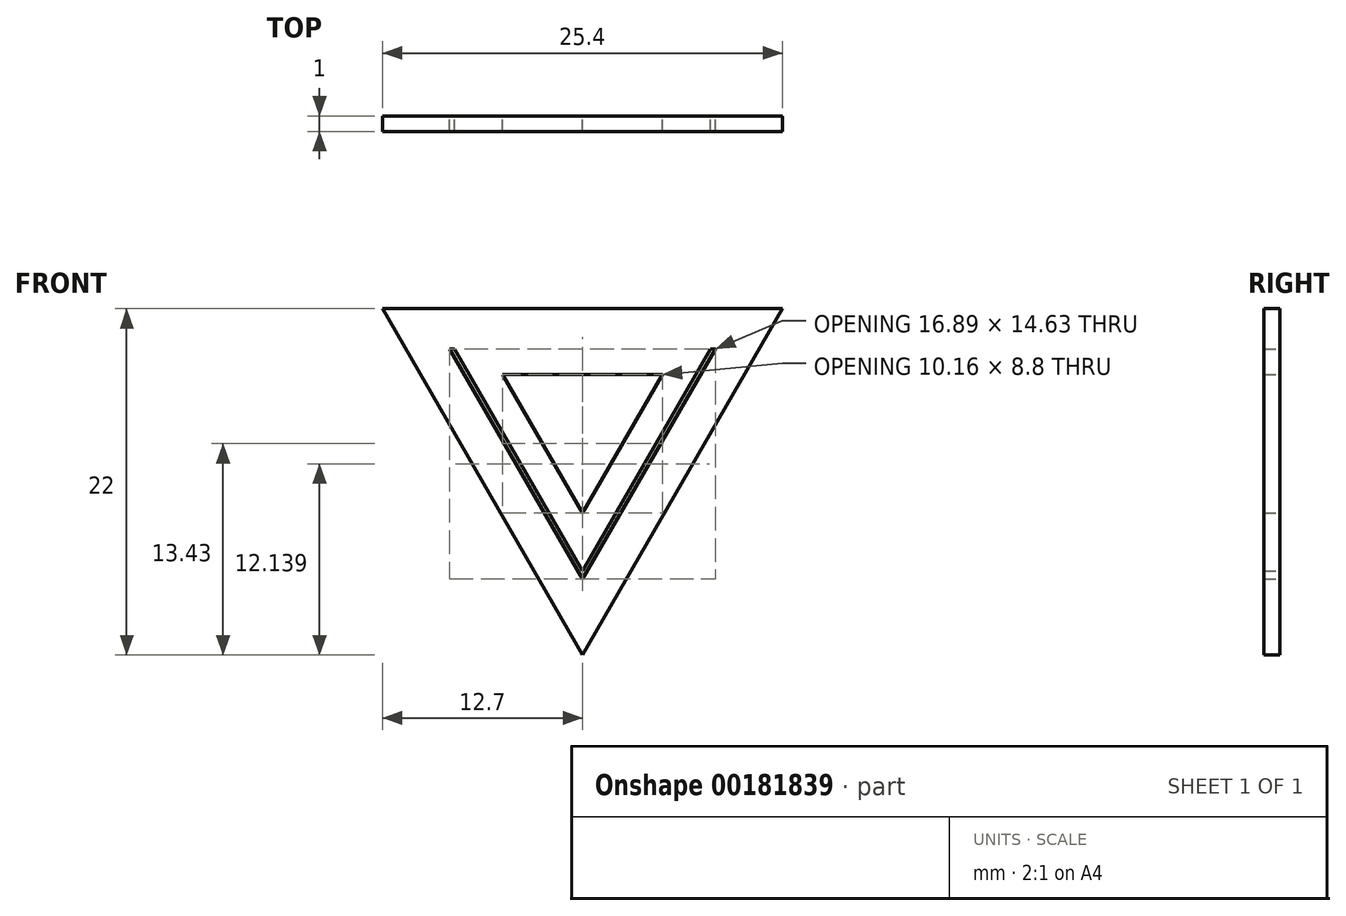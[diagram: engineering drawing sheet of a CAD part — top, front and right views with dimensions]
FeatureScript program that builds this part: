
annotation { "Feature Type Name" : "Feature", "Feature Type Description" : "" }
export const myFeature = defineFeature(function(context is Context, id is Id, definition is map)
    precondition{}
    {
        {
            var Q0;
            Q0=qCreatedBy(makeId("Front.planeOp"),FACE);
            var sketch = newSketch(context, id + "F0", { "sketchPlane" : qUnion([Q0])});
            skLineSegment(sketch, "E0", {"start": v(-12.7, 0) * mm, "end": v(12.7, 0) * mm});
            skLineSegment(sketch, "E1", {"start": v(12.7, 0) * mm, "end": v(0, -22) * mm});
            skLineSegment(sketch, "E2", {"start": v(0, -22) * mm, "end": v(-12.7, 0) * mm});
            skLineSegment(sketch, "E3", {"start": v(-8.45, -2.55) * mm, "end": v(0, -17.17) * mm});
            skLineSegment(sketch, "E4", {"start": v(0, -17.17) * mm, "end": v(8.45, -2.55) * mm});
            skLineSegment(sketch, "E5", {"start": v(-5.08, -4.17) * mm, "end": v(5.08, -4.17) * mm});
            skLineSegment(sketch, "E6", {"start": v(5.08, -4.17) * mm, "end": v(0, -12.97) * mm});
            skLineSegment(sketch, "E7", {"start": v(0, -12.97) * mm, "end": v(-5.08, -4.17) * mm});
            skLineSegment(sketch, "E8", {"start": v(8.45, -2.55) * mm, "end": v(0, -17.17) * mm});
            skLineSegment(sketch, "E9", {"start": v(-8.14, -2.55) * mm, "end": v(0, -16.65) * mm});
            skLineSegment(sketch, "E10", {"start": v(0, -16.65) * mm, "end": v(8.14, -2.55) * mm});
            skLineSegment(sketch, "E11", {"start": v(8.14, -2.55) * mm, "end": v(8.45, -2.55) * mm});
            skLineSegment(sketch, "E12", {"start": v(-8.45, -2.55) * mm, "end": v(-8.14, -2.55) * mm});
            skSolve(sketch);
        }
        {
            var Q0;
            Q0=makeQuery(id+"F0.imprint","IMPRINT",FACE,{"disambiguationData":[TD([[makeQuery(id+"F0.imprint","IMPRINT",EDGE,{"derivedFrom":sQuery(id+"F0.wireOp",EDGE,"E0")}),-1.0]])]});
            extrude(context, id + "F1", {"entities" : qUnion([Q0]), "depth" : 1 * mm});
        }
    });
